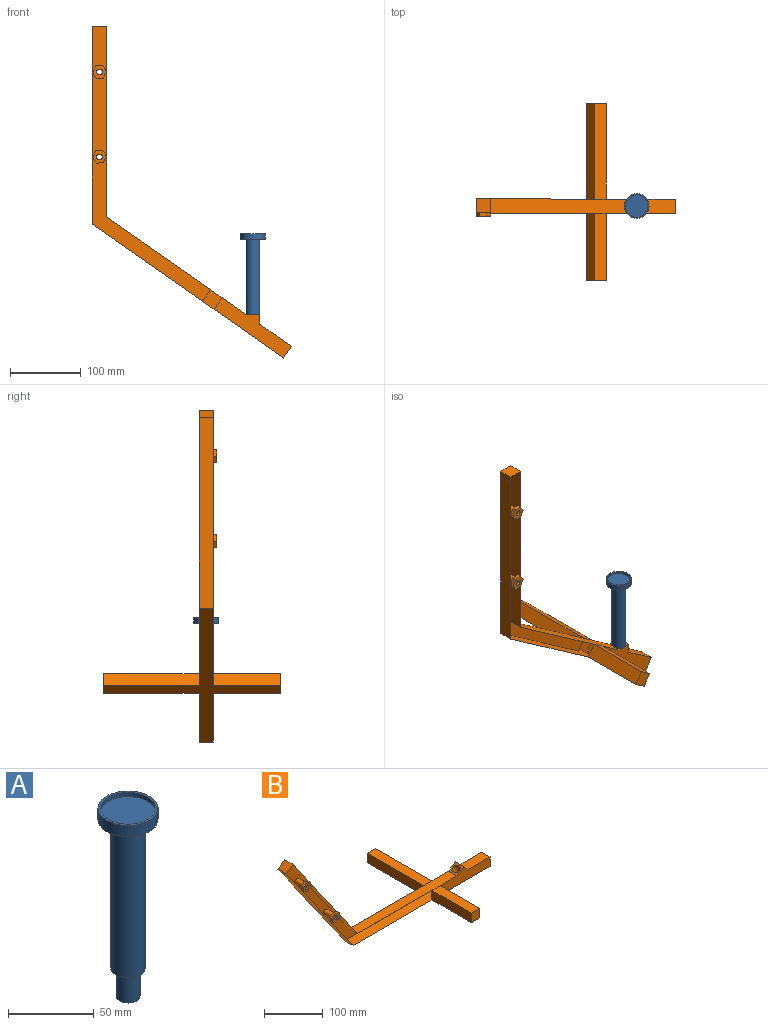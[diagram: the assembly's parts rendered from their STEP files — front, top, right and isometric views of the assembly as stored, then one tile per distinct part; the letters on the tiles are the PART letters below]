
ASSEMBLY  parts=2 mates=1
PART A: 9 faces, bbox 35x35x134 mm
  f0: cylinder r=7mm len=20mm, axis (0,0,-1), area 879.6mm2, adj f1,f3
  f1: plane 14x14mm, normal (0,0,-1), area 153.9mm2, adj f0
  f2: cylinder r=10mm len=106mm, axis (0,0,-1), area 6660.2mm2, adj f3,f5
  f3: plane 20x20mm, normal (0,0,-1), area 160.2mm2, adj f0,f2
  f4: cylinder r=17.5mm len=35mm, axis (0,0,-1), area 879.6mm2, adj f5,f7
  f5: plane 35x35mm, normal (0,0,-1), area 648mm2, adj f2,f4
  f6: cylinder r=16mm len=32mm, axis (0,0,-1), area 301.6mm2, adj f7,f8
  f7: plane 35x35mm, normal (0,0,1), area 157.9mm2, adj f4,f6
  f8: plane 32x32mm, normal (0,0,1), area 804.2mm2, adj f6
PART B: 45 faces, bbox 490.7x250x241.2 mm
  f0: plane 55x20mm, normal (0,0,1), area 1100mm2, adj f2,f4,f10,f40
  f1: plane 350.79x241.22mm, normal (0,-1,0), area 8683.8mm2, adj f5,f6,f7,f8,f9,f13,f19,f23
  f2: plane 119.92x31.47mm, normal (0,-1,0), area 2537.9mm2, adj f0,f9,f10,f13,f21,f40,f41,f42
  f3: plane 350.79x241.22mm, normal (0,1,0), area 9043.1mm2, adj f5,f6,f7,f8,f9,f11,f12,f13
  f4: plane 119.92x31.47mm, normal (0,1,0), area 2537.9mm2, adj f0,f9,f10,f13,f15,f40,f41,f42
  f5: plane 221.23x154.8mm, normal (0.82,0,0.57), area 5400.2mm2, adj f1,f3,f6,f13
  f6: plane 20x16.35mm, normal (-0.57,0,0.82), area 399.1mm2, adj f1,f3,f5,f7
  f7: plane 20x8.55mm, normal (-0.82,0,-0.57), area 208.2mm2, adj f1,f3,f6,f8
  f8: plane 221.23x154.8mm, normal (-0.82,0,-0.57), area 5400.2mm2, adj f1,f3,f7,f9
  f9: plane 329.98x250mm, normal (0,0,-1), area 11199.6mm2, adj f1,f2,f3,f4,f8,f10,f14,f15
  f10: plane 20x19.99mm, normal (1,0,0), area 399.9mm2, adj f0,f2,f4,f9
  f11: cylinder r=5.01mm len=20mm, axis (0,1,0), area 629.6mm2, adj f3,f22
  f12: cylinder r=4.99mm len=20mm, axis (0,1,0), area 627.3mm2, adj f3,f31
  f13: plane 240.16x20.01mm, normal (0,0,1), area 4803mm2, adj f1,f2,f3,f4,f5,f17,f18,f42
  f14: plane 20x20mm, normal (0,1,0), area 400mm2, adj f9,f15,f16,f17
  f15: plane 135x20mm, normal (1,0,0), area 2700.1mm2, adj f4,f9,f14,f17
  f16: plane 135x20mm, normal (-1,0,0), area 2700.1mm2, adj f3,f9,f14,f17
  f17: plane 135.01x20.01mm, normal (0,0,1), area 2700.1mm2, adj f13,f14,f15,f16
  f18: plane 95.01x20.01mm, normal (0,0,1), area 1899.9mm2, adj f13,f19,f20,f21
  f19: plane 95x20mm, normal (-1,0,0), area 1899.9mm2, adj f1,f9,f18,f20
  f20: plane 20x20mm, normal (0,-1,0), area 400mm2, adj f9,f18,f19,f21
  f21: plane 95x20mm, normal (1,0,0), area 1899.9mm2, adj f2,f9,f18,f20
  f22: plane 10.02x10.02mm, normal (0,1,0), area 28mm2, adj f11,f29
  f23: plane 8.08x5.85mm, normal (0.59,0,-0.81), area 49.9mm2, adj f1,f24,f28,f30
  f24: plane 9.93x5mm, normal (0.99,0,0.1), area 49.9mm2, adj f1,f23,f25,f30
  f25: plane 9.11x5mm, normal (0.41,0,0.91), area 49.9mm2, adj f1,f24,f26,f30
  f26: plane 8.08x5.85mm, normal (-0.59,0,0.81), area 49.9mm2, adj f1,f25,f27,f30
  f27: plane 9.93x5mm, normal (-0.99,0,-0.1), area 49.9mm2, adj f1,f26,f28,f30
  f28: plane 9.11x5mm, normal (-0.41,0,-0.91), area 49.9mm2, adj f1,f23,f27,f30
  f29: cylinder r=4.02mm len=8.05mm, axis (0,1,0), area 126.4mm2, adj f22,f30
  f30: plane 19.85x18.22mm, normal (0,-1,0), area 207.8mm2, adj f23,f24,f25,f26,f27,f28,f29
  f31: plane 9.98x9.98mm, normal (0,1,0), area 28.2mm2, adj f12,f37
  f32: plane 7.91x6.06mm, normal (0.61,0,-0.79), area 49.8mm2, adj f1,f33,f38,f39
  f33: plane 9.88x5mm, normal (0.99,0,0.13), area 49.8mm2, adj f1,f32,f34,f39
  f34: plane 9.2x5mm, normal (0.38,0,0.92), area 49.8mm2, adj f1,f33,f35,f39
  f35: plane 7.91x6.06mm, normal (-0.61,0,0.79), area 49.8mm2, adj f1,f34,f36,f39
  f36: plane 9.88x5mm, normal (-0.99,0,-0.13), area 49.8mm2, adj f1,f35,f38,f39
  f37: cylinder r=3.99mm len=7.99mm, axis (0,1,0), area 125.5mm2, adj f31,f39
  f38: plane 9.2x5mm, normal (-0.38,0,-0.92), area 49.8mm2, adj f1,f32,f36,f39
  f39: plane 19.75x18.4mm, normal (0,-1,0), area 207.7mm2, adj f32,f33,f34,f35,f36,f37,f38
  f40: plane 20x11.48mm, normal (0.82,0,0.57), area 280.2mm2, adj f0,f2,f4,f41
  f41: plane 20x16.38mm, normal (-0.57,0,0.82), area 246.1mm2, adj f2,f4,f40,f42,f44
  f42: plane 20x0.01mm, normal (-0.82,0,-0.57), area 0.2mm2, adj f2,f4,f13,f41
  f43: cone r=0mm half-angle=59deg, axis (-0.57,0,0.82), area 179.6mm2, adj f44
  f44: cylinder r=7mm len=24.41mm, axis (-0.57,0,0.82), area 879.6mm2, adj f41,f43
PLACE A t=(61.92,34.19,36.58)mm
PLACE B rot(axis=(0,1,0),35deg) t=(-164.8,44.19,183.91)mm
MATE planar A.f0 <-> B.f44  axis (0,0,-1) through (61.92,34.19,36.58)mm
